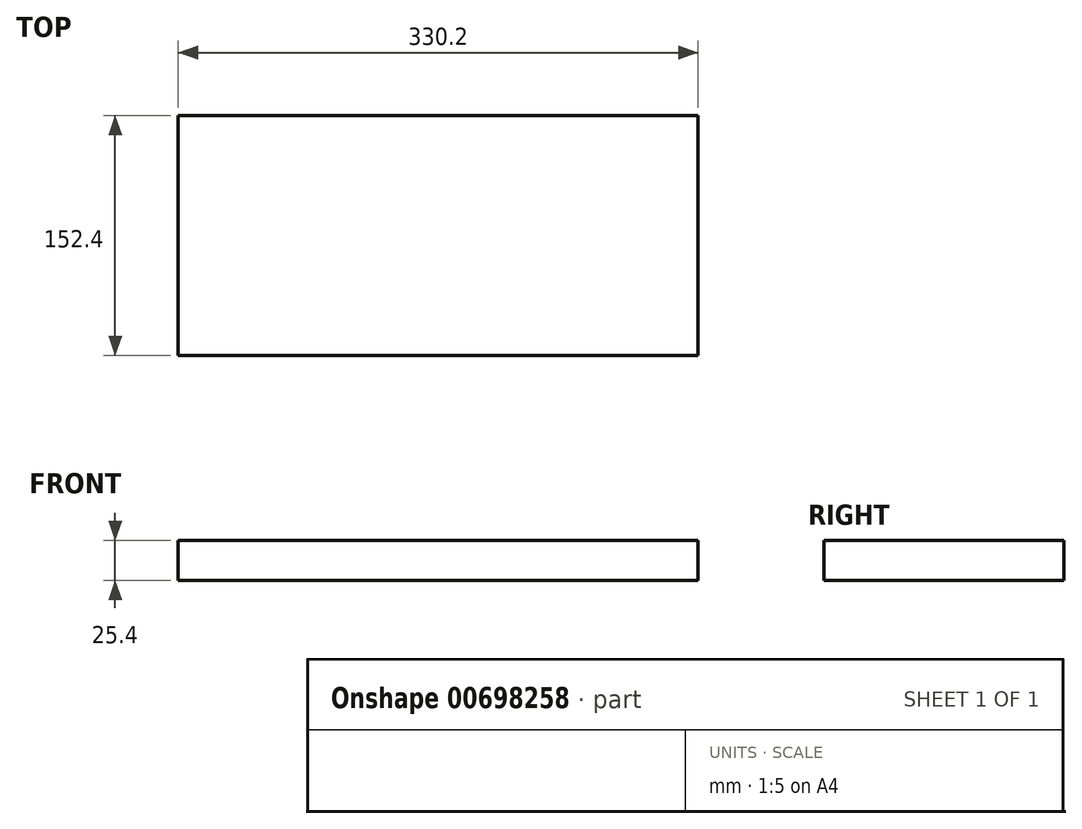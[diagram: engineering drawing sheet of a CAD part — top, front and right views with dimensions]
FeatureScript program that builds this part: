
annotation { "Feature Type Name" : "Feature", "Feature Type Description" : "" }
export const myFeature = defineFeature(function(context is Context, id is Id, definition is map)
    precondition{}
    {
        {
            var Q0;
            Q0=qCreatedBy(makeId("Top.planeOp"),FACE);
            var sketch = newSketch(context, id + "F0", { "sketchPlane" : qUnion([Q0])});
            skLineSegment(sketch, "E0.bottom", {"start": v(190.57, -116.28) * mm, "end": v(-139.63, -116.28) * mm});
            skLineSegment(sketch, "E0.top", {"start": v(190.57, 36.12) * mm, "end": v(-139.63, 36.12) * mm});
            skLineSegment(sketch, "E0.left", {"start": v(190.57, -116.28) * mm, "end": v(190.57, 36.12) * mm});
            skLineSegment(sketch, "E0.right", {"start": v(-139.63, -116.28) * mm, "end": v(-139.63, 36.12) * mm});
            skSolve(sketch);
        }
        {
            var Q0;
            Q0=makeQuery(id+"F0.imprint","IMPRINT",FACE,{"disambiguationData":[TD([[makeQuery(id+"F0.imprint","IMPRINT",EDGE,{"derivedFrom":sQuery(id+"F0.wireOp",EDGE,"E0.bottom")}),-1.0]])]});
            extrude(context, id + "F1", {"entities" : qUnion([Q0]), "depth" : 25.4 * mm, "offsetDistance" : 25.4 * mm});
        }
    });
